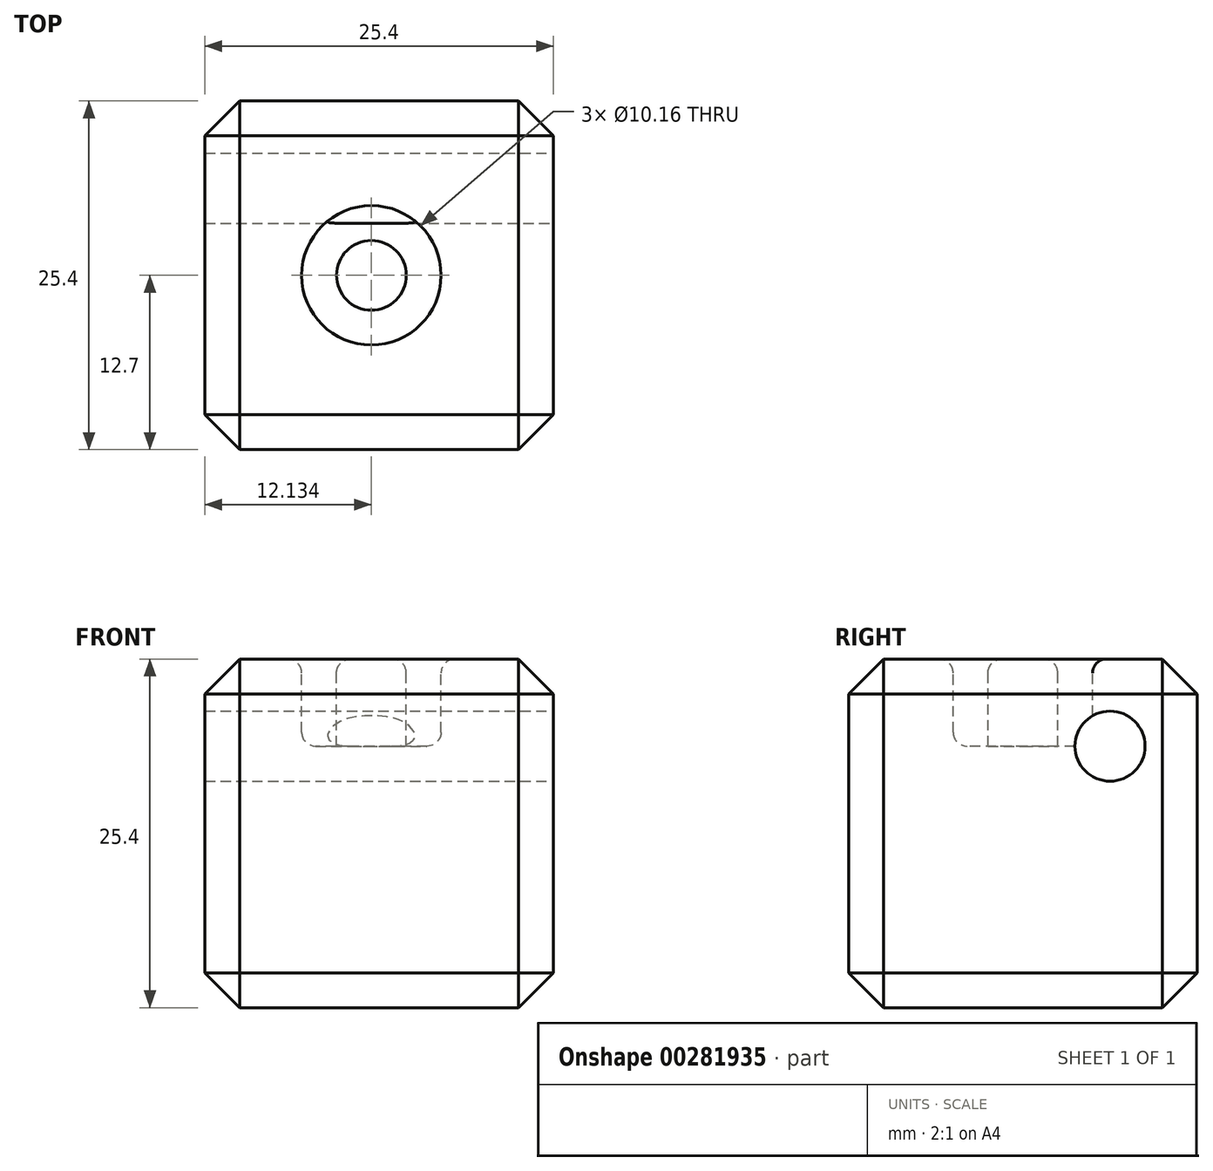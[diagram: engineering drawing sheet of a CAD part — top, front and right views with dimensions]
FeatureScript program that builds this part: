
annotation { "Feature Type Name" : "Feature", "Feature Type Description" : "" }
export const myFeature = defineFeature(function(context is Context, id is Id, definition is map)
    precondition{}
    {
        {
            var Q0;
            Q0=qCreatedBy(makeId("Top.planeOp"),FACE);
            var sketch = newSketch(context, id + "F0", { "sketchPlane" : qUnion([Q0])});
            skLineSegment(sketch, "E0.bottom", {"start": v(0, 0) * mm, "end": v(25.4, 0) * mm});
            skLineSegment(sketch, "E0.top", {"start": v(0, 25.4) * mm, "end": v(25.4, 25.4) * mm});
            skLineSegment(sketch, "E0.left", {"start": v(0, 0) * mm, "end": v(0, 25.4) * mm});
            skLineSegment(sketch, "E0.right", {"start": v(25.4, 0) * mm, "end": v(25.4, 25.4) * mm});
            skSolve(sketch);
        }
        {
            var Q0;
            Q0=makeQuery(id+"F0.imprint","IMPRINT",FACE,{"disambiguationData":[TD([[makeQuery(id+"F0.imprint","IMPRINT",EDGE,{"derivedFrom":sQuery(id+"F0.wireOp",EDGE,"E0.bottom")}),1.0]])]});
            extrude(context, id + "F1", {"entities" : qUnion([Q0]), "depth" : 25.4 * mm});
        }
        {
            var Q0;
            Q0=makeQuery(id+"F1.opExtrude","CAP_FACE",FACE,{"disambiguationData":[OSD([sQuery(id+"F0.wireOp",EDGE,"E0.bottom"),sQuery(id+"F0.wireOp",EDGE,"E0.top"),sQuery(id+"F0.wireOp",EDGE,"E0.left"),sQuery(id+"F0.wireOp",EDGE,"E0.right")])],"isStart":false});
            var sketch = newSketch(context, id + "F2", { "sketchPlane" : qUnion([Q0])});
            skCircle(sketch, "E1", {"center": v(12.13, 12.7) * mm, "radius": 5.08 * mm});
            skPoint(sketch, "E1.centerSnap0", {"position": v(12.13, 25.4) * mm});
            skCircle(sketch, "E2", {"center": v(12.13, 12.7) * mm, "radius": 2.54 * mm});
            skSolve(sketch);
        }
        {
            var Q0;
            Q0=makeQuery(id+"F2.imprint","IMPRINT",FACE,{"disambiguationData":[TD([[makeQuery(id+"F2.imprint","IMPRINT",EDGE,{"derivedFrom":sQuery(id+"F2.wireOp",EDGE,"E1")}),1.0]])]});
            var Q1;
            Q1=sQuery(id+"F2.wireOp",EDGE,"E1");
            extrude(context, id + "F3", {"entities" : qUnion([Q0]), "operationType" : NewBodyOperationType.REMOVE, "surfaceEntities" : qUnion([Q1]), "oppositeDirection" : true, "depth" : 6.35 * mm});
        }
        {
            var Q0;
            Q0=makeQuery(id+"F3.boolean.opBoolean","COPY",EDGE,{"derivedFrom":makeQuery(id+"F3.opExtrude","CAP_EDGE",EDGE,{"disambiguationData":[OSD([sQuery(id+"F2.wireOp",EDGE,"E2")])],"isStart":true})});
            var Q1;
            Q1=makeQuery(id+"F3.boolean.opBoolean","COPY",FACE,{"derivedFrom":makeQuery(id+"F3.opExtrude","SWEPT_FACE",FACE,{"disambiguationData":[OSD([sQuery(id+"F2.wireOp",EDGE,"E1")])]})});
            var Q2;
            Q2=makeQuery(id+"F3.boolean.opBoolean","COPY",EDGE,{"derivedFrom":makeQuery(id+"F3.opExtrude","CAP_EDGE",EDGE,{"disambiguationData":[OSD([sQuery(id+"F2.wireOp",EDGE,"E1")])],"isStart":false})});
            fillet(context, id + "F4", {"entities" : qUnion([Q0, Q1, Q2]), "radius" : 1.02 * mm, "tangentPropagation" : true, "allowEdgeOverflow" : false});
        }
        {
            var Q0;
            Q0=makeQuery(id+"F1.opExtrude","CAP_EDGE",EDGE,{"disambiguationData":[OSD([sQuery(id+"F0.wireOp",EDGE,"E0.right")])],"isStart":false});
            var Q1;
            Q1=makeQuery(id+"F1.opExtrude","SWEPT_FACE",FACE,{"disambiguationData":[OSD([sQuery(id+"F0.wireOp",EDGE,"E0.top")])]});
            var Q2;
            Q2=makeQuery(id+"F1.opExtrude","CAP_EDGE",EDGE,{"disambiguationData":[OSD([sQuery(id+"F0.wireOp",EDGE,"E0.bottom")])],"isStart":false});
            var Q3;
            Q3=makeQuery(id+"F1.opExtrude","CAP_EDGE",EDGE,{"disambiguationData":[OSD([sQuery(id+"F0.wireOp",EDGE,"E0.left")])],"isStart":false});
            var Q4;
            Q4=makeQuery(id+"F1.opExtrude","SWEPT_FACE",FACE,{"disambiguationData":[OSD([sQuery(id+"F0.wireOp",EDGE,"E0.bottom")])]});
            var Q5;
            Q5=makeQuery(id+"F1.opExtrude","CAP_FACE",FACE,{"disambiguationData":[OSD([sQuery(id+"F0.wireOp",EDGE,"E0.bottom"),sQuery(id+"F0.wireOp",EDGE,"E0.top"),sQuery(id+"F0.wireOp",EDGE,"E0.left"),sQuery(id+"F0.wireOp",EDGE,"E0.right")])],"isStart":true});
            chamfer(context, id + "F5", {"entities" : qUnion([Q0, Q1, Q2, Q3, Q4, Q5]), "width" : 2.54 * mm, "tangentPropagation" : true});
        }
        {
            var Q0;
            Q0=makeQuery(id+"F1.opExtrude","SWEPT_FACE",FACE,{"disambiguationData":[OSD([sQuery(id+"F0.wireOp",EDGE,"E0.right")])]});
            var sketch = newSketch(context, id + "F6", { "sketchPlane" : qUnion([Q0])});
            skPoint(sketch, "E3", {"position": v(19.05, 19.05) * mm});
            skSolve(sketch);
        }
        {
            var Q0;
            Q0=sQuery(id+"F6.wireOp",VERTEX,"E3");
            var Q1;
            Q1=makeQuery(id+"F1.opExtrude","SWEPT_BODY",BODY,{"disambiguationData":[OSD([sQuery(id+"F0.wireOp",EDGE,"E0.bottom"),sQuery(id+"F0.wireOp",EDGE,"E0.top"),sQuery(id+"F0.wireOp",EDGE,"E0.left"),sQuery(id+"F0.wireOp",EDGE,"E0.right")])]});
            hole(context, id + "F7", {"style" : HoleStyle.SIMPLE, "endStyle" : HoleEndStyle.THROUGH, "standardTappedOrClearance" : lookupTablePath({ "standard" : "ANSI", "engagement" : "75%", "pitch" : "20 tpi", "size" : "1/4", "type" : "Tapped" }), "standardBlindInLast" : lookupTablePath({ "standard" : "ANSI", "engagement" : "75%", "pitch" : "20 tpi", "size" : "1/4", "type" : "Tapped" }), "holeDiameter" : 5.1 * mm, "showTappedDepth" : true, "tappedDepth" : 12.7 * mm, "tapClearance" : 3, "locations" : qUnion([Q0]), "scope" : qUnion([Q1]), "majorDiameter" : 6.35 * mm});
        }
    });
